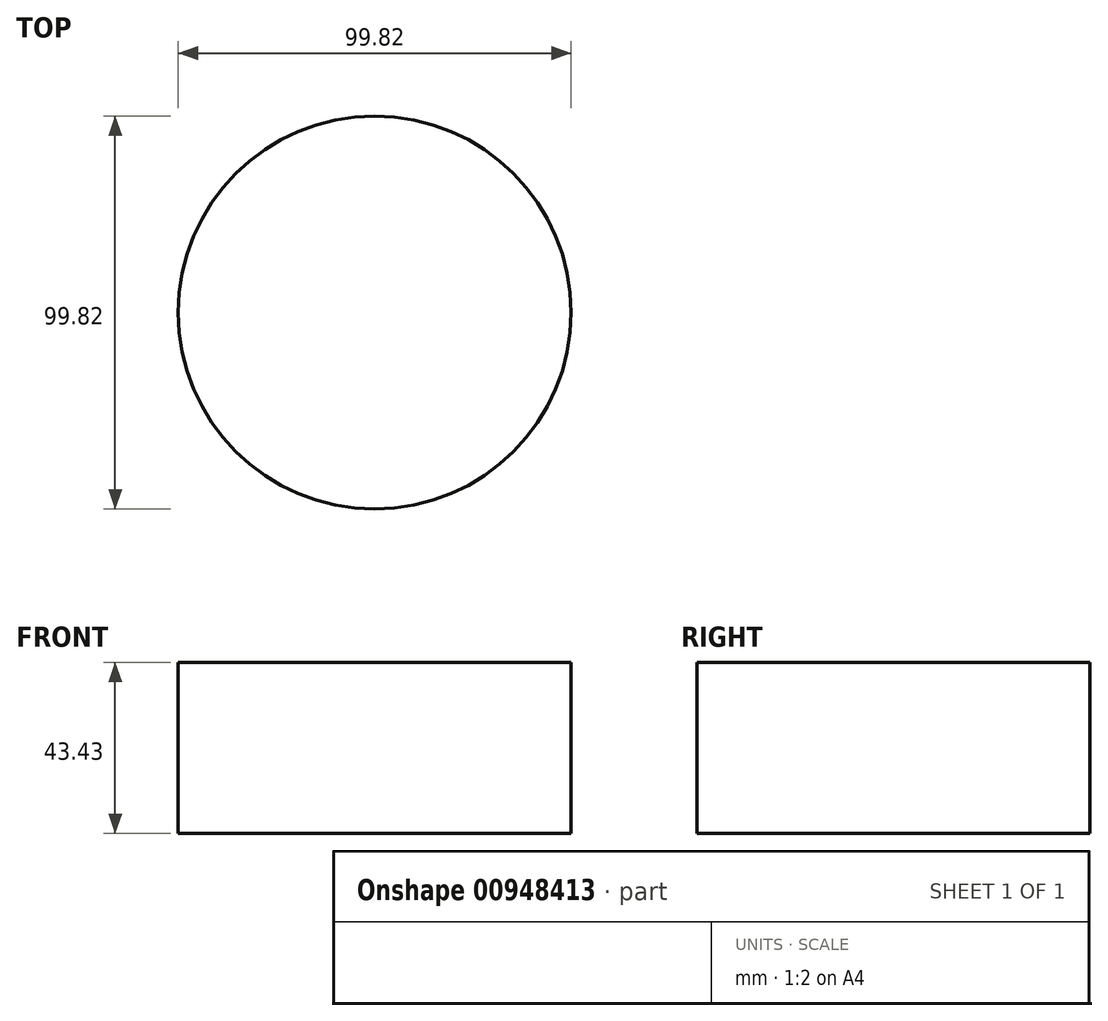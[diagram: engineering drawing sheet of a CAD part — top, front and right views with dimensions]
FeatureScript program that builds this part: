
annotation { "Feature Type Name" : "Feature", "Feature Type Description" : "" }
export const myFeature = defineFeature(function(context is Context, id is Id, definition is map)
    precondition{}
    {
        {
            var Q0;
            Q0=qCreatedBy(makeId("Top.planeOp"),FACE);
            var sketch = newSketch(context, id + "F0", { "sketchPlane" : qUnion([Q0])});
            skCircle(sketch, "E0", {"center": v(0, 0) * mm, "radius": 49.91 * mm});
            skSolve(sketch);
        }
        {
            var Q0;
            Q0 = qSketchRegion(id + "F0", true);
            extrude(context, id + "F1", {"entities" : qUnion([Q0]), "depth" : 43.43 * mm, "offsetDistance" : 25.4 * mm});
        }
    });
